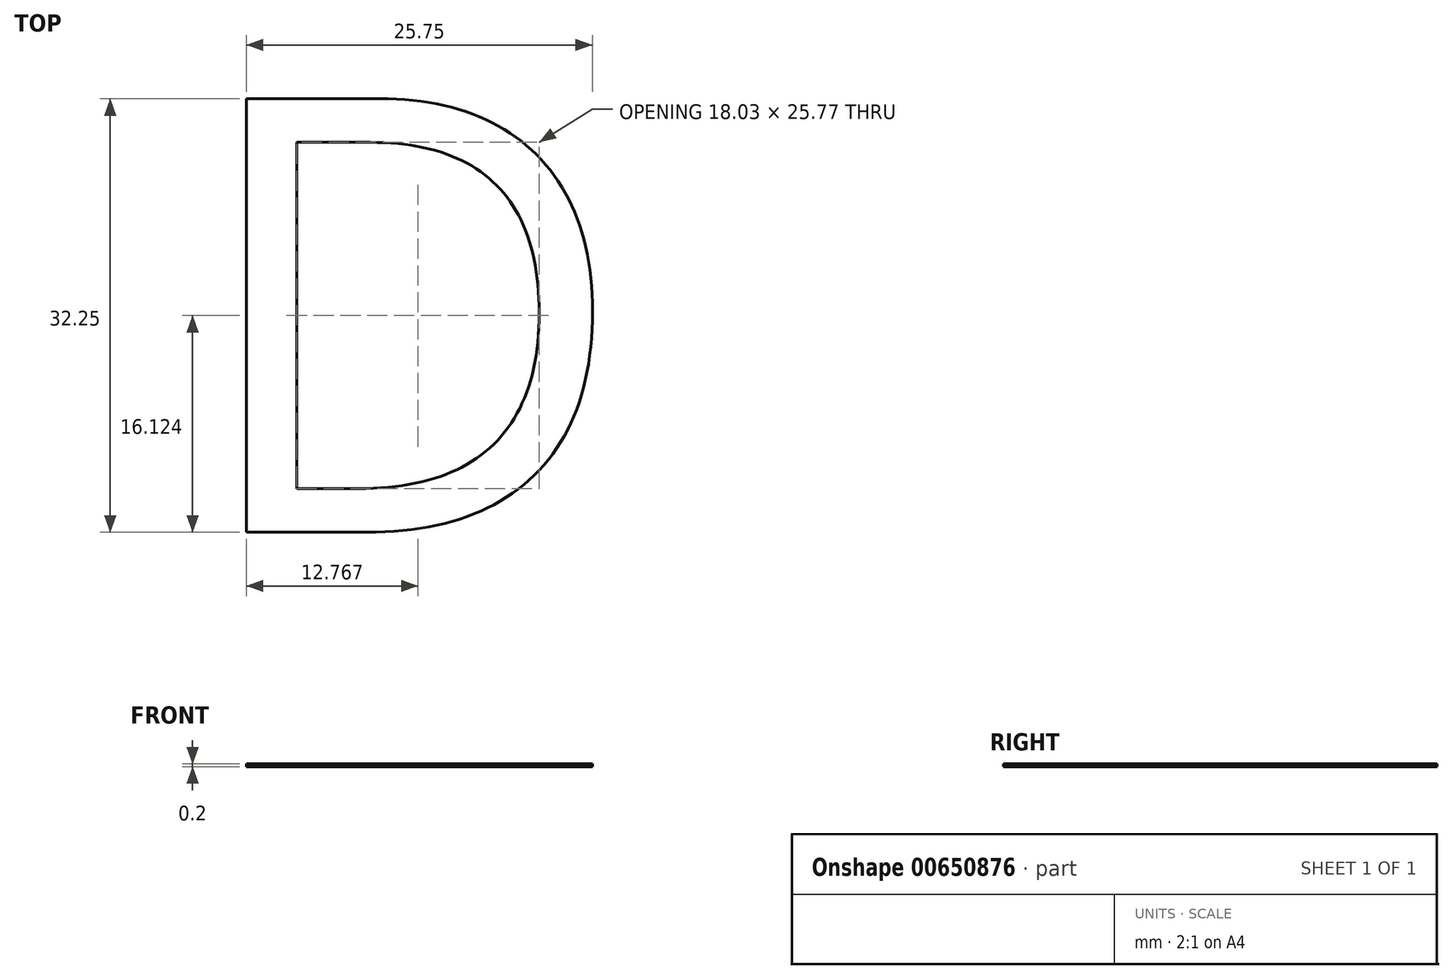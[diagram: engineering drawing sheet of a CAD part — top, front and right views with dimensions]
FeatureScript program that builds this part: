
annotation { "Feature Type Name" : "Feature", "Feature Type Description" : "" }
export const myFeature = defineFeature(function(context is Context, id is Id, definition is map)
    precondition{}
    {
        {
            var Q0;
            Q0=qCreatedBy(makeId("Top.planeOp"),FACE);
            var sketch = newSketch(context, id + "F0", { "sketchPlane" : qUnion([Q0])});
            skText(sketch, "E0", { "text": "D", "fontName": "OpenSans-Regular.ttf"});
            const initialGuessF0  = {"E0": [-0.01655, -0.03253, 1, 0, 0.03253]};
            skSetInitialGuess(sketch, initialGuessF0);
            skSolve(sketch);
        }
        {
            var Q0;
            Q0=makeQuery(id+"F0.imprint","IMPRINT",FACE,{"disambiguationData":[TD([[makeQuery(id+"F0.imprint","IMPRINT",EDGE,{"derivedFrom":sQuery(id+"F0.wireOp",EDGE,"E0.sketch_text.stroke-0")}),-1.0]])]});
            extrude(context, id + "F1", {"entities" : qUnion([Q0]), "depth" : 0.2 * mm, "offsetDistance" : 25.4 * mm});
        }
    });
